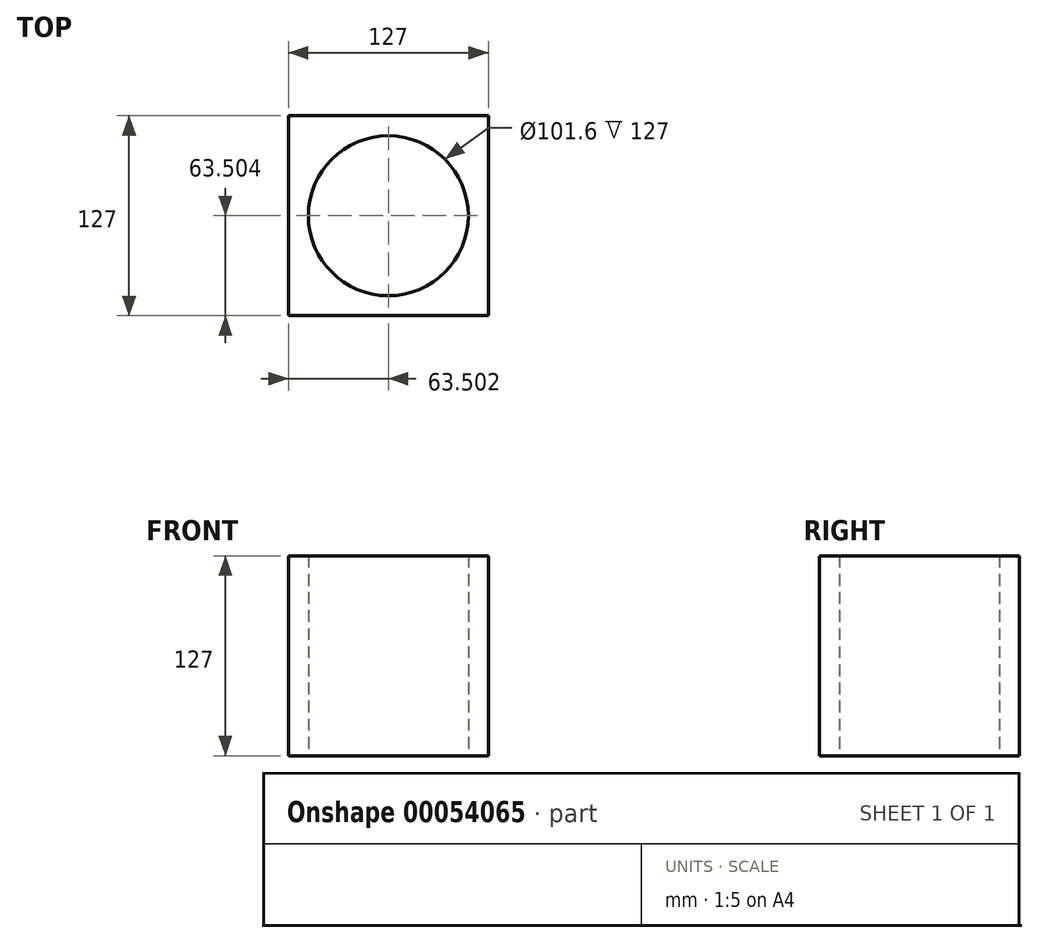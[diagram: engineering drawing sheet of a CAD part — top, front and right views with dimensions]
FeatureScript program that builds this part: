
annotation { "Feature Type Name" : "Feature", "Feature Type Description" : "" }
export const myFeature = defineFeature(function(context is Context, id is Id, definition is map)
    precondition{}
    {
        {
            var Q0;
            Q0=qCreatedBy(makeId("Top.planeOp"),FACE);
            var sketch = newSketch(context, id + "F0", { "sketchPlane" : qUnion([Q0])});
            skLineSegment(sketch, "E0.bottom", {"start": v(-94.4, 87.23) * mm, "end": v(32.6, 87.23) * mm});
            skLineSegment(sketch, "E0.top", {"start": v(-94.4, -39.77) * mm, "end": v(32.6, -39.77) * mm});
            skLineSegment(sketch, "E0.left", {"start": v(-94.4, 87.23) * mm, "end": v(-94.4, -39.77) * mm});
            skLineSegment(sketch, "E0.right", {"start": v(32.6, 87.23) * mm, "end": v(32.6, -39.77) * mm});
            skLineSegment(sketch, "E1", {"start": v(-94.4, 87.23) * mm, "end": v(32.6, -39.77) * mm, "construction": true});
            skCircle(sketch, "E2", {"center": v(-30.9, 23.73) * mm, "radius": 50.8 * mm});
            skSolve(sketch);
        }
        {
            var Q0;
            Q0=makeQuery(id+"F0.imprint","IMPRINT",FACE,{"disambiguationData":[TD([[makeQuery(id+"F0.imprint","IMPRINT",EDGE,{"derivedFrom":sQuery(id+"F0.wireOp",EDGE,"E0.bottom")}),-1.0]])]});
            extrude(context, id + "F1", {"entities" : qUnion([Q0]), "depth" : 127 * mm});
        }
        {
            var Q0;
            Q0=makeQuery(id+"F0.imprint","IMPRINT",FACE,{"disambiguationData":[TD([[makeQuery(id+"F0.imprint","IMPRINT",EDGE,{"derivedFrom":sQuery(id+"F0.wireOp",EDGE,"E0.bottom")}),-1.0]])]});
            extrude(context, id + "F2", {"entities" : qUnion([Q0]), "operationType" : NewBodyOperationType.ADD, "depth" : 127 * mm});
        }
    });
